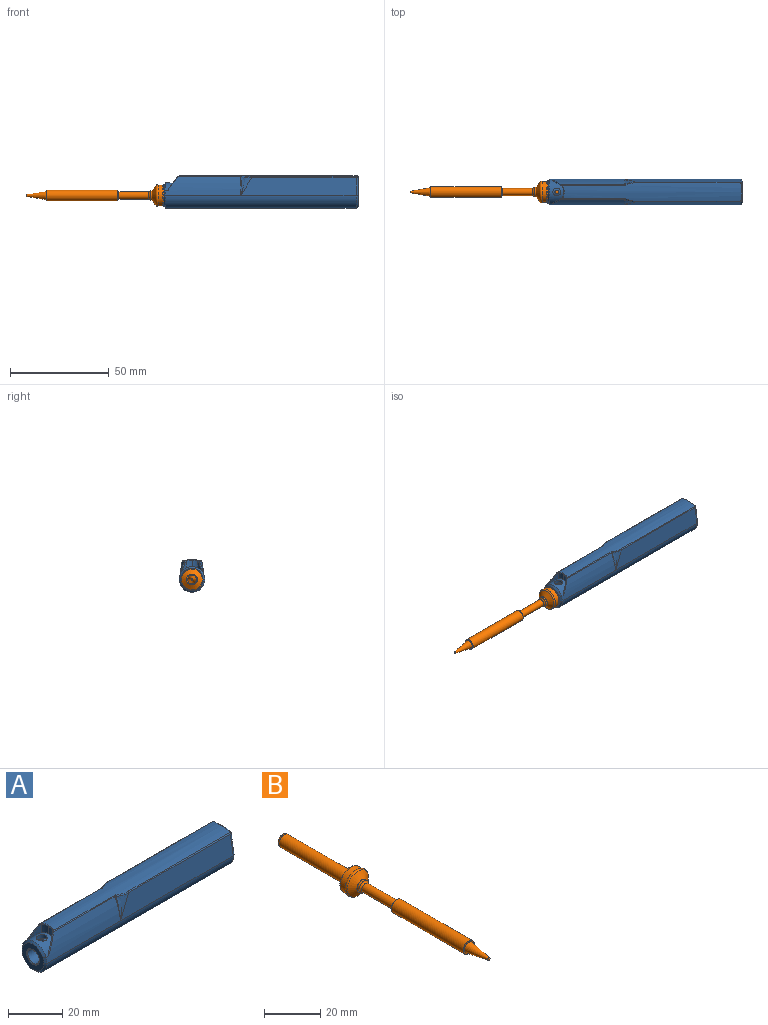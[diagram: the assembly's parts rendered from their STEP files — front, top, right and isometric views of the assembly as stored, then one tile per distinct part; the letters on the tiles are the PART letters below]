
ASSEMBLY  parts=2 mates=1
PART A: 53 faces, bbox 98.5x14.3x21.6 mm
  f0: cylinder r=20mm len=90.52mm, axis (-1,0,0), area 753.2mm2, adj f1,f10,f11,f12,f13,f14,f21,f22
  f1: cylinder r=0.5mm len=31.83mm, axis (-1,0,0), area 15.5mm2, adj f0,f15,f25,f44,f45
  f2: plane 15.05x11mm, normal (1,0,0), area 103.5mm2, adj f7,f8,f9,f12,f34
  f3: cylinder r=6.5mm len=96.7mm, axis (-1,0,0), area 1974.6mm2, adj f5,f6,f8,f15,f16,f48
  f4: plane 11.4x11.4mm, normal (-1,0,0), area 67.6mm2, adj f28,f46,f47,f48,f49
  f5: plane 58.5x9.09mm, normal (0,0.99,0.16), area 511.7mm2, adj f3,f9,f10,f19
  f6: plane 58.5x9.09mm, normal (0,-0.99,0.16), area 511.7mm2, adj f3,f7,f14,f20
  f7: cylinder r=1mm len=9.44mm, axis (0,0.16,0.99), area 14.5mm2, adj f2,f6,f8,f13
  f8: torus R=5.5mm, axis (1,0,0), area 30.2mm2, adj f2,f3,f7,f9
  f9: cylinder r=1mm len=9.44mm, axis (0,0.16,-0.99), area 14.5mm2, adj f2,f5,f8,f11
  f10: cylinder r=0.5mm len=52.85mm, axis (-1,0,0), area 31.1mm2, adj f0,f5,f11,f21
  f11: bspline ~1.26x1.07mm, area 0.8mm2, adj f0,f9,f10,f12
  f12: torus R=19.5mm, axis (1,0,0), area 6.5mm2, adj f0,f2,f11,f13
  f13: bspline ~1.26x1.23mm, area 0.8mm2, adj f0,f7,f12,f14
  f14: cylinder r=0.5mm len=52.85mm, axis (-1,0,0), area 31.1mm2, adj f0,f6,f13,f24
  f15: cylinder r=36.33mm len=38.2mm, axis (-1,0,0), area 351.9mm2, adj f1,f3,f17,f35,f42,f49
  f16: cylinder r=36.33mm len=38.2mm, axis (-1,0,0), area 351.9mm2, adj f3,f18,f23,f35,f40,f46
  f17: torus R=37.33mm, axis (1,0,0), area 2.1mm2, adj f15,f20,f25
  f18: torus R=37.33mm, axis (1,0,0), area 2.1mm2, adj f16,f19,f22
  f19: bspline ~14.54x7.13mm, area 20.1mm2, adj f5,f18,f21
  f20: bspline ~14.54x7.13mm, area 20.1mm2, adj f6,f17,f24
  f21: bspline ~7.29x2.9mm, area 2.9mm2, adj f0,f10,f19,f22
  f22: bspline ~1x0.53mm, area 0.3mm2, adj f0,f18,f21,f23
  f23: cylinder r=0.5mm len=31.83mm, axis (-1,0,0), area 15.5mm2, adj f0,f16,f22,f41,f43
  f24: bspline ~7.15x1.92mm, area 2.9mm2, adj f0,f14,f20,f25
  f25: bspline ~0.99x0.65mm, area 0.3mm2, adj f0,f1,f17,f24
  f26: cylinder r=3mm len=34.7mm, axis (-1,0,0), area 650.9mm2, adj f27,f28,f52
  f27: plane 6x6mm, normal (-1,0,0), area 28.3mm2, adj f26
  f28: cone r=3.3mm half-angle=45deg, axis (-1,0,0), area 8.4mm2, adj f4,f26
  f29: cylinder r=2.75mm len=19.5mm, axis (1,0,0), area 336.9mm2, adj f30,f34
  f30: plane 5.5x5.5mm, normal (1,0,0), area 18.8mm2, adj f29,f31
  f31: cylinder r=1.25mm len=19.5mm, axis (1,0,0), area 153.2mm2, adj f30,f33
  f32: plane 1.5x1.5mm, normal (1,0,0), area 1.8mm2, adj f33
  f33: torus R=0.75mm, axis (1,0,0), area 5.3mm2, adj f31,f32
  f34: torus R=3.25mm, axis (1,0,0), area 14.5mm2, adj f2,f29
  f35: cylinder r=6.5mm len=12.05mm, axis (-1,0,0), area 61.4mm2, adj f15,f16,f36,f37,f38,f39,f40,f42
  f36: cylinder r=6.5mm len=4.03mm, axis (0,0,1), area 10.8mm2, adj f35,f37,f39,f44,f45
  f37: cylinder r=6.5mm len=4.03mm, axis (0,0,1), area 10.8mm2, adj f35,f36,f38,f41,f43
  f38: cylinder r=22mm len=5.56mm, axis (0,0,1), area 9.4mm2, adj f35,f37,f40,f41
  f39: cylinder r=22mm len=5.56mm, axis (0,0,1), area 9.4mm2, adj f35,f36,f42,f44
  f40: bspline ~9.74x7.83mm, area 5.2mm2, adj f16,f35,f38,f41
  f41: bspline ~1.07x0.72mm, area 0.3mm2, adj f23,f37,f38,f40,f43
  f42: bspline ~9.74x7.83mm, area 5.2mm2, adj f15,f35,f39,f44
  f43: bspline ~5.6x1.85mm, area 1.3mm2, adj f0,f23,f37,f41,f45
  f44: bspline ~1.07x0.72mm, area 0.3mm2, adj f1,f36,f39,f42,f45
  f45: bspline ~4.88x1.79mm, area 1.3mm2, adj f0,f1,f36,f43,f44
  f46: cone r=36.33mm half-angle=45deg, axis (1,0,0), area 2.7mm2, adj f4,f16,f47,f48
  f47: cone r=5.7mm half-angle=45deg, axis (1,0,0), area 16.3mm2, adj f4,f35,f46,f49
  f48: cone r=6.5mm half-angle=45deg, axis (1,0,0), area 21.6mm2, adj f3,f4,f46,f49
  f49: cone r=36.33mm half-angle=45deg, axis (1,0,0), area 2.7mm2, adj f4,f15,f47,f48
  f50: cylinder r=2mm len=4mm, axis (0,0,1), area 23.5mm2, adj f35,f51
  f51: cylinder r=3mm len=4mm, axis (-1,0,0), area 10.2mm2, adj f50,f52
  f52: cylinder r=1mm len=2mm, axis (0,0,1), area 12.6mm2, adj f26,f51
PART B: 18 faces, bbox 12x104x12 mm
  f0: cone r=2.5mm half-angle=54.5deg, axis (0,1,0), area 84.3mm2, adj f1,f17
  f1: cylinder r=2.5mm len=5mm, axis (0,1,0), area 15.7mm2, adj f0,f2
  f2: torus R=2.5mm, axis (0,1,0), area 14.2mm2, adj f1,f3
  f3: cylinder r=1.8mm len=15.1mm, axis (0,1,0), area 170.8mm2, adj f2,f4
  f4: torus R=2.5mm, axis (0,1,0), area 14.2mm2, adj f3,f5
  f5: plane 5.5x5.5mm, normal (0,1,0), area 4.1mm2, adj f4,f6
  f6: cylinder r=2.75mm len=36mm, axis (0,1,0), area 622mm2, adj f5,f7
  f7: plane 5.5x5.5mm, normal (0,-1,0), area 9.2mm2, adj f6,f8
  f8: cone r=2.15mm half-angle=9.3deg, axis (0,1,0), area 84.8mm2, adj f7,f9
  f9: sphere r=0.5mm, area 1.3mm2, adj f8
  f10: plane 3.3x3.3mm, normal (0,1,0), area 8.6mm2, adj f11
  f11: torus R=1.65mm, axis (0,1,0), area 22.6mm2, adj f10,f12
  f12: cylinder r=2.65mm len=32.8mm, axis (0,1,0), area 546.1mm2, adj f11,f13
  f13: torus R=2.85mm, axis (0,1,0), area 5.4mm2, adj f12,f14
  f14: plane 9.6x9.6mm, normal (0,1,0), area 46.9mm2, adj f13,f15
  f15: torus R=4.8mm, axis (0,1,0), area 25.3mm2, adj f14,f16
  f16: cylinder r=5.3mm len=10.6mm, axis (0,1,0), area 83.3mm2, adj f15,f17
  f17: torus R=4.94mm, axis (0,1,0), area 40.1mm2, adj f0,f16
PLACE A t=(-0.3,0,0)mm
PLACE B rot(axis=(-0.58,-0.58,-0.58),120deg) t=(33.7,0,0)mm
MATE fastened A.f26 <-> B.f0  axis (-1,0,0) through (-0.3,0,0)mm
